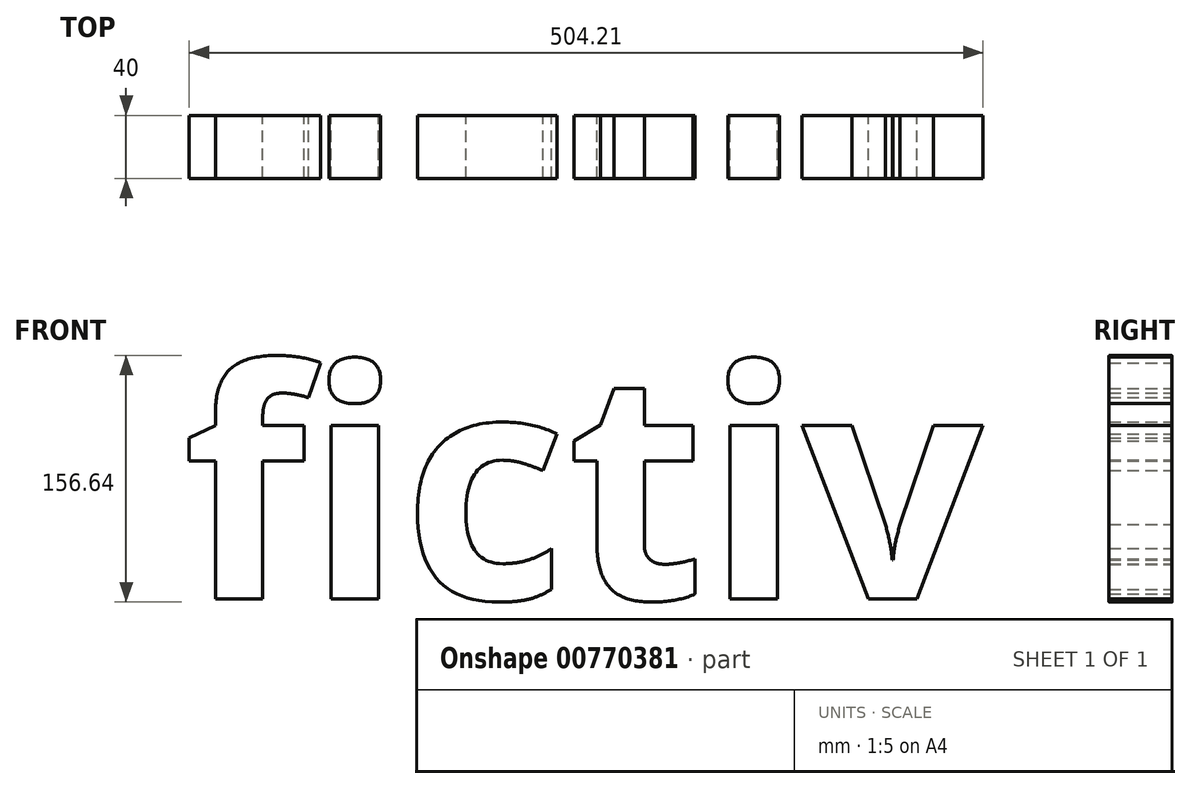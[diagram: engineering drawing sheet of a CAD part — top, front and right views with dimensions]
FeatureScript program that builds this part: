
annotation { "Feature Type Name" : "Feature", "Feature Type Description" : "" }
export const myFeature = defineFeature(function(context is Context, id is Id, definition is map)
    precondition{}
    {
        {
            var Q0;
            Q0=qCreatedBy(makeId("Front.planeOp"),FACE);
            var sketch = newSketch(context, id + "F0", { "sketchPlane" : qUnion([Q0])});
            skText(sketch, "E0", { "text": "fictiv", "fontName": "OpenSans-Bold.ttf"});
            const initialGuessF0  = {"E0": [-0.26474, -0.07291, 1, 0, 0.14552]};
            skSetInitialGuess(sketch, initialGuessF0);
            skSolve(sketch);
        }
        {
            var Q0;
            Q0 = qSketchRegion(id + "F0", true);
            extrude(context, id + "F1", {"entities" : qUnion([Q0]), "depth" : 40 * mm, "offsetDistance" : 25 * mm});
        }
    });
